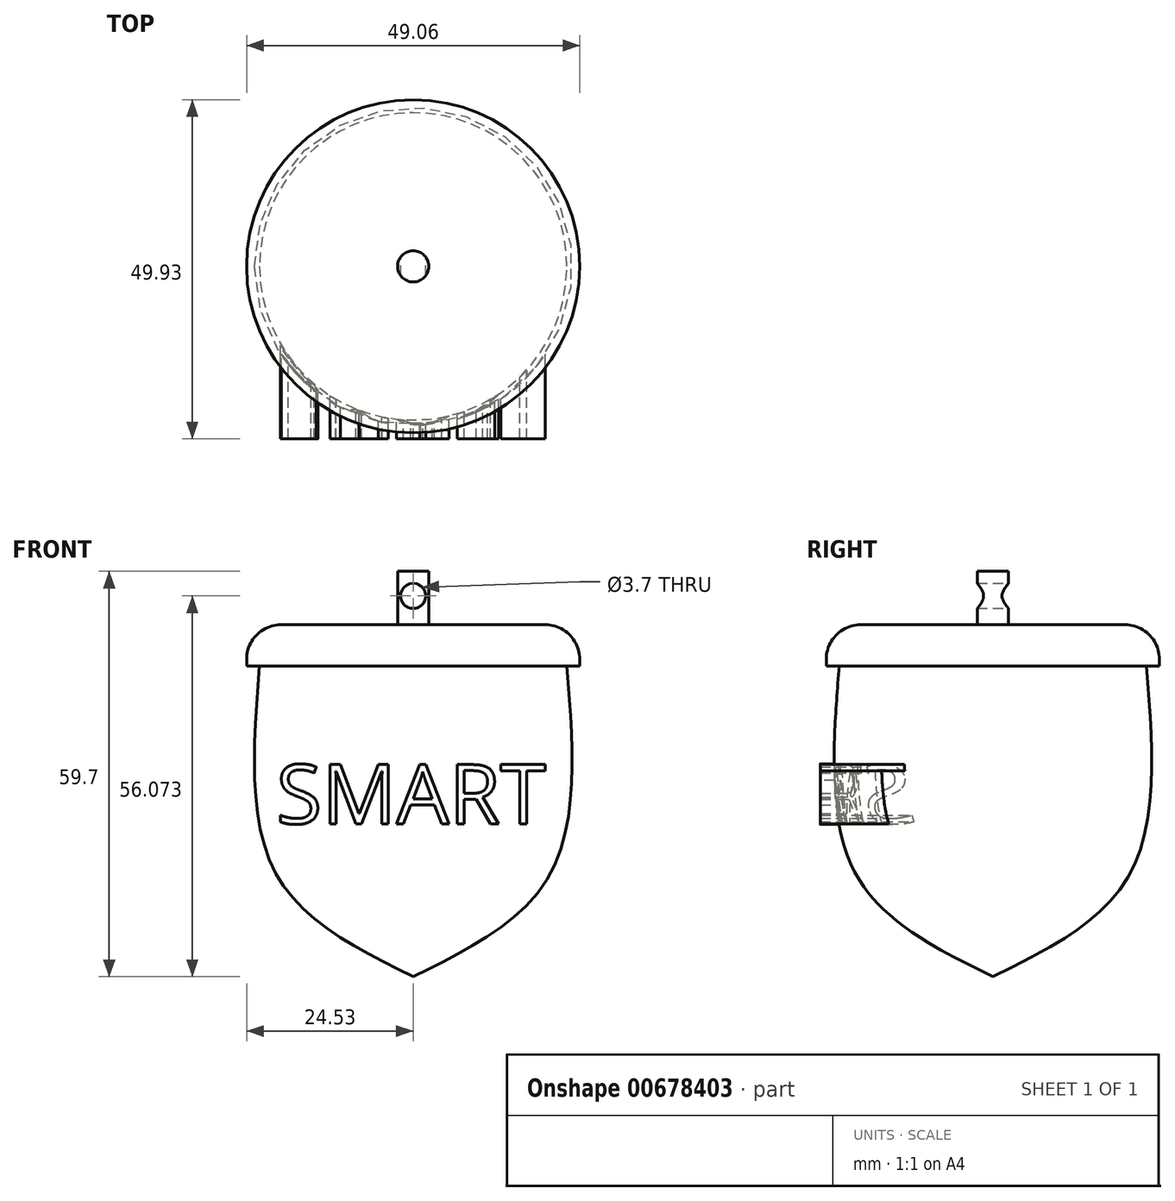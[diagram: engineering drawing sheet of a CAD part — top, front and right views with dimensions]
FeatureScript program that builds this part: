
annotation { "Feature Type Name" : "Feature", "Feature Type Description" : "" }
export const myFeature = defineFeature(function(context is Context, id is Id, definition is map)
    precondition{}
    {
        {
            var Q0;
            Q0=qCreatedBy(makeId("Front.planeOp"),FACE);
            var sketch = newSketch(context, id + "F0", { "sketchPlane" : qUnion([Q0])});
            skFitSpline(sketch, "E0", {"points": [v(0, 0) * mm, v(-22.63, 0) * mm], "startDerivative": vector(-22.63, 0) * mm, "endDerivative": vector(-22.63, 0) * mm});
            skFitSpline(sketch, "E1", {"points": [v(-22.63, 0) * mm, v(-20.15, -30.65) * mm, v(0, -45.73) * mm], "startDerivative": vector(-5.16, -65.36) * mm, "endDerivative": vector(51.36, -25.44) * mm});
            skLineSegment(sketch, "E2", {"start": v(0, 0) * mm, "end": v(0, -45.73) * mm});
            skSolve(sketch);
        }
        {
            var Q0;
            Q0 = qSketchRegion(id + "F0", true);
            var Q1;
            Q1=sQuery(id+"F0.wireOp",EDGE,"E2");
            revolve(context, id + "F1", {"entities" : qUnion([Q0]), "axis" : qUnion([Q1]), "revolveType" : RevolveType.FULL});
        }
        {
            var Q0;
            Q0=qCreatedBy(makeId("Front.planeOp"),FACE);
            var sketch = newSketch(context, id + "F2", { "sketchPlane" : qUnion([Q0])});
            skLineSegment(sketch, "E3", {"start": v(0, 0) * mm, "end": v(0, -20.11) * mm});
            skText(sketch, "E4", { "text": "SMART", "fontName": "OpenSans-Regular.ttf"});
            skLineSegment(sketch, "E5", {"start": v(0, 0) * mm, "end": v(0, 13.59) * mm});
            const initialGuessF2  = {"E4": [-0.02015, -0.0232, 1, 0, 0.00878]};
            skSetInitialGuess(sketch, initialGuessF2);
            skSolve(sketch);
        }
        {
            var Q0;
            Q0 = qSketchRegion(id + "F2", true);
            extrude(context, id + "F3", {"entities" : qUnion([Q0]), "operationType" : NewBodyOperationType.ADD, "depth" : 25.4 * mm, "offsetDistance" : 25.4 * mm});
        }
        {
            var Q0;
            Q0=makeQuery(id+"F1.opRevolve","SWEPT_FACE",FACE,{"disambiguationData":[OSD([sQuery(id+"F0.wireOp",EDGE,"E0")])]});
            var sketch = newSketch(context, id + "F4", { "sketchPlane" : qUnion([Q0])});
            skCircle(sketch, "E6", {"center": v(0, 0) * mm, "radius": 24.53 * mm});
            skSolve(sketch);
        }
        {
            var Q0;
            Q0 = qSketchRegion(id + "F4", true);
            extrude(context, id + "F5", {"entities" : qUnion([Q0]), "operationType" : NewBodyOperationType.ADD, "depth" : 6.1 * mm, "offsetDistance" : 25.4 * mm});
        }
        {
            var Q0;
            Q0=makeQuery(id+"F5.opExtrude","CAP_EDGE",EDGE,{"disambiguationData":[OSD([sQuery(id+"F4.wireOp",EDGE,"E6")])],"isStart":false});
            fillet(context, id + "F6", {"entities" : qUnion([Q0]), "radius" : 5.08 * mm, "tangentPropagation" : true, "allowEdgeOverflow" : false});
        }
        {
            var Q0;
            Q0=makeQuery(id+"F5.opExtrude","CAP_FACE",FACE,{"disambiguationData":[OSD([sQuery(id+"F4.wireOp",EDGE,"E6")])],"isStart":false});
            var sketch = newSketch(context, id + "F7", { "sketchPlane" : qUnion([Q0])});
            skCircle(sketch, "E7", {"center": v(0, 0) * mm, "radius": 2.3 * mm});
            skSolve(sketch);
        }
        {
            var Q0;
            Q0 = qSketchRegion(id + "F7", true);
            extrude(context, id + "F8", {"entities" : qUnion([Q0]), "operationType" : NewBodyOperationType.ADD, "depth" : 7.87 * mm, "offsetDistance" : 25.4 * mm});
        }
        {
            var Q0;
            Q0=qCreatedBy(makeId("Front.planeOp"),FACE);
            var sketch = newSketch(context, id + "F9", { "sketchPlane" : qUnion([Q0])});
            skLineSegment(sketch, "E8", {"start": v(0, 0) * mm, "end": v(0, 38.03) * mm});
            skCircle(sketch, "E9", {"center": v(0, 10.34) * mm, "radius": 1.85 * mm});
            skSolve(sketch);
        }
        {
            var Q0;
            Q0 = qSketchRegion(id + "F9", true);
            extrude(context, id + "F10", {"entities" : qUnion([Q0]), "operationType" : NewBodyOperationType.REMOVE, "depth" : 17.53 * mm, "offsetDistance" : 25.4 * mm, "hasSecondDirection" : true, "secondDirectionOppositeDirection" : true, "secondDirectionDepth" : 25.4 * mm});
        }
    });
